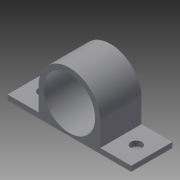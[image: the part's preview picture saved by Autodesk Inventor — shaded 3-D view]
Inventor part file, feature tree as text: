
AUTODESK INVENTOR PART (.ipt)
format: ipt  version: 2013 (Build 170138000, 138)  size: 109,056 bytes
history: native  units: in
note: dims shown in document units (in); Inventor stores cm internally (conversion verified against a paired STEP export)
features: extrude x2, sketch x2
ambient origin geometry x8: Origin, YZ Plane, XZ Plane, XY Plane, X Axis, Y Axis, Z Axis, Center Point
bodies: Solid1 (feature_tree)
feature tree (4):
  extrude  "Extrusion1"  Depth=1.5in
  extrude  "Extrusion2"  Depth=0.6875in
  sketch  "Sketch1"  dims[d0=1.5in d1=1.5in]
  sketch  "Sketch2"  dims[d2=0.125in d3=0.6875in d4=1.25in d5=0.125in d6=1.0in d7=0.0in d8=0.266in d11=1.0in d12=0.0in d13=0.375in d14=0.266in d15=0.375in]
